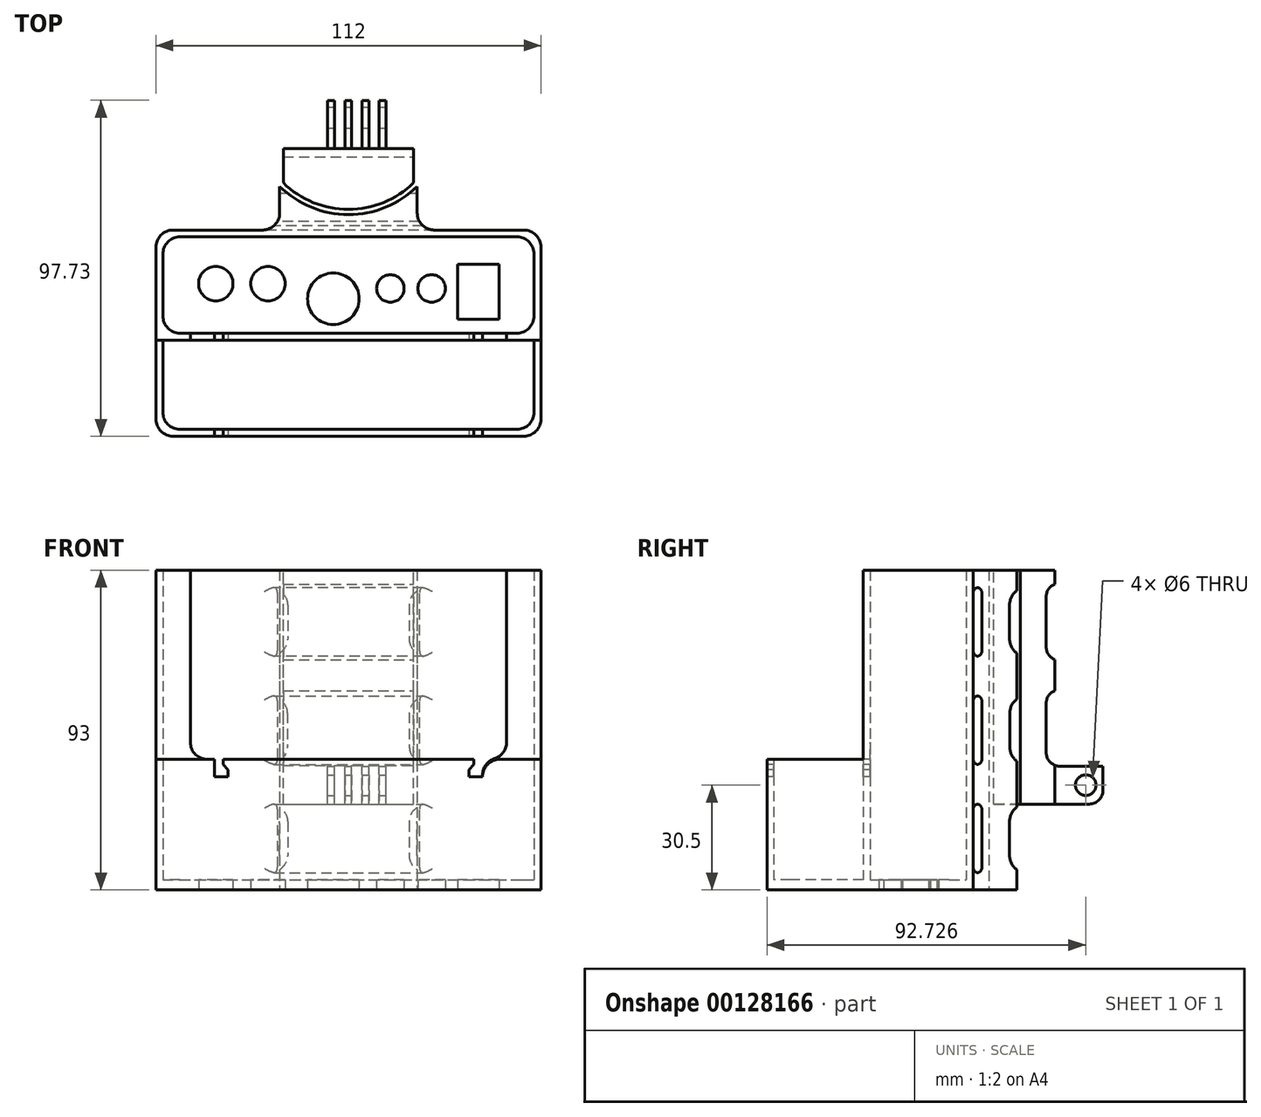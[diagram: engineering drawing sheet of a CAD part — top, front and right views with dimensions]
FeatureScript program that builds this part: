
annotation { "Feature Type Name" : "Feature", "Feature Type Description" : "" }
export const myFeature = defineFeature(function(context is Context, id is Id, definition is map)
    precondition{}
    {
        {
            var Q0;
            Q0=qCreatedBy(makeId("Top.planeOp"),FACE);
            var sketch = newSketch(context, id + "F0", { "sketchPlane" : qUnion([Q0])});
            skLineSegment(sketch, "E0.bottom", {"start": v(-47.35, 13.6) * mm, "end": v(60.65, 13.6) * mm});
            skLineSegment(sketch, "E0.top", {"start": v(-47.35, -14.4) * mm, "end": v(60.65, -14.4) * mm});
            skLineSegment(sketch, "E0.left", {"start": v(-47.35, 13.6) * mm, "end": v(-47.35, -14.4) * mm});
            skLineSegment(sketch, "E0.right", {"start": v(60.65, 13.6) * mm, "end": v(60.65, -14.4) * mm});
            skLineSegment(sketch, "E1.bottom", {"start": v(-49.35, 15.6) * mm, "end": v(62.65, 15.6) * mm});
            skLineSegment(sketch, "E1.top", {"start": v(-49.35, -16.4) * mm, "end": v(62.65, -16.4) * mm});
            skLineSegment(sketch, "E1.left", {"start": v(-49.35, 15.6) * mm, "end": v(-49.35, -16.4) * mm});
            skLineSegment(sketch, "E1.right", {"start": v(62.65, 15.6) * mm, "end": v(62.65, -16.4) * mm});
            skLineSegment(sketch, "E2", {"start": v(-49.35, -16.4) * mm, "end": v(-49.35, -44.4) * mm});
            skLineSegment(sketch, "E3", {"start": v(-49.35, -44.4) * mm, "end": v(62.65, -44.4) * mm});
            skLineSegment(sketch, "E4", {"start": v(62.65, -44.4) * mm, "end": v(62.65, -16.4) * mm});
            skLineSegment(sketch, "E5", {"start": v(-47.35, -16.4) * mm, "end": v(-47.35, -42.4) * mm});
            skLineSegment(sketch, "E6", {"start": v(-47.35, -42.4) * mm, "end": v(60.65, -42.4) * mm});
            skLineSegment(sketch, "E7", {"start": v(60.65, -42.4) * mm, "end": v(60.65, -16.4) * mm});
            skCircle(sketch, "E8", {"center": v(-31.95, 0) * mm, "radius": 5 * mm});
            skCircle(sketch, "E9", {"center": v(-16.75, 0) * mm, "radius": 5 * mm});
            skCircle(sketch, "E10", {"center": v(2.25, -4.4) * mm, "radius": 7.5 * mm});
            skCircle(sketch, "E11", {"center": v(30.85, -1.4) * mm, "radius": 4 * mm});
            skLineSegment(sketch, "E12.bottom", {"start": v(50.45, -10.4) * mm, "end": v(38.45, -10.4) * mm});
            skLineSegment(sketch, "E12.top", {"start": v(50.45, 5.6) * mm, "end": v(38.45, 5.6) * mm});
            skLineSegment(sketch, "E12.left", {"start": v(50.45, -10.4) * mm, "end": v(50.45, 5.6) * mm});
            skLineSegment(sketch, "E12.right", {"start": v(38.45, -10.4) * mm, "end": v(38.45, 5.6) * mm});
            skCircle(sketch, "E13", {"center": v(18.85, -1.4) * mm, "radius": 4 * mm});
            skLineSegment(sketch, "E14", {"start": v(6.65, 15.6) * mm, "end": v(6.65, 20.1) * mm});
            skLineSegment(sketch, "E15", {"start": v(-13.35, 28.25) * mm, "end": v(-13.35, 15.6) * mm});
            skArc(sketch, "E16", {"start": v(-13.35, 28.25) * mm, "mid": v(-4.15, 22.22) * mm, "end": v(6.65, 20.1) * mm});
            skArc(sketch, "E17.MirrorCS", {"start": v(26.65, 28.25) * mm, "mid": v(17.45, 22.22) * mm, "end": v(6.65, 20.1) * mm});
            skLineSegment(sketch, "E18.MirrorCS", {"start": v(26.65, 28.25) * mm, "end": v(26.65, 15.6) * mm});
            skSolve(sketch);
        }
        {
            var Q0;
            Q0=makeQuery(id+"F0.imprint","IMPRINT",FACE,{"disambiguationData":[TD([[makeQuery(id+"F0.imprint","IMPRINT",EDGE,{"derivedFrom":sQuery(id+"F0.wireOp",EDGE,"E0.bottom")}),-1.0]])]});
            var Q1;
            {var subQ0=sQuery(id+"F0.wireOp",EDGE,"E5");Q1=makeQuery(id+"F0.imprint","IMPRINT",FACE,{"disambiguationData":[TD([[makeQuery(id+"F0.imprint","IMPRINT",EDGE,{"derivedFrom":subQ0}),1.0]])]});}
            extrude(context, id + "F1", {"entities" : qUnion([Q0, Q1]), "depth" : 3 * mm});
        }
        {
            var Q0;
            Q0=makeQuery(id+"F0.imprint","IMPRINT",FACE,{"disambiguationData":[TD([[makeQuery(id+"F0.imprint","IMPRINT",EDGE,{"derivedFrom":sQuery(id+"F0.wireOp",EDGE,"E0.bottom")}),1.0]])]});
            var Q1;
            {var subQ0=sQuery(id+"F0.wireOp",EDGE,"E14");Q1=makeQuery(id+"F0.imprint","IMPRINT",FACE,{"disambiguationData":[TD([[makeQuery(id+"F0.imprint","IMPRINT",EDGE,{"derivedFrom":subQ0}),1.0]])]});}
            var Q2;
            {var subQ0=sQuery(id+"F0.wireOp",EDGE,"E14");Q2=makeQuery(id+"F0.imprint","IMPRINT",FACE,{"disambiguationData":[TD([[makeQuery(id+"F0.imprint","IMPRINT",EDGE,{"derivedFrom":subQ0}),-1.0]])]});}
            extrude(context, id + "F2", {"entities" : qUnion([Q0, Q1, Q2]), "operationType" : NewBodyOperationType.ADD, "depth" : 93 * mm});
        }
        {
            var Q0;
            Q0=makeQuery(id+"F2.opExtrude","SWEPT_FACE",FACE,{"disambiguationData":[OSD([sQuery(id+"F0.wireOp",EDGE,"E1.top")])]});
            var sketch = newSketch(context, id + "F3", { "sketchPlane" : qUnion([Q0])});
            skLineSegment(sketch, "E19.bottom", {"start": v(52.65, 93) * mm, "end": v(-39.35, 93) * mm});
            skLineSegment(sketch, "E19.top", {"start": v(52.65, 38) * mm, "end": v(-39.35, 38) * mm});
            skLineSegment(sketch, "E19.left", {"start": v(52.65, 93) * mm, "end": v(52.65, 38) * mm});
            skLineSegment(sketch, "E19.right", {"start": v(-39.35, 93) * mm, "end": v(-39.35, 38) * mm});
            skSolve(sketch);
        }
        {
            var Q0;
            Q0=makeQuery(id+"F3.imprint","IMPRINT",FACE,{"disambiguationData":[TD([[makeQuery(id+"F3.imprint","IMPRINT",EDGE,{"derivedFrom":sQuery(id+"F3.wireOp",EDGE,"E19.bottom")}),-1.0]])]});
            extrude(context, id + "F4", {"entities" : qUnion([Q0]), "operationType" : NewBodyOperationType.REMOVE, "oppositeDirection" : true, "depth" : 2 * mm});
        }
        {
            var Q0;
            {var subQ0=sQuery(id+"F0.wireOp",EDGE,"E2");Q0=makeQuery(id+"F0.imprint","IMPRINT",FACE,{"disambiguationData":[TD([[makeQuery(id+"F0.imprint","IMPRINT",EDGE,{"derivedFrom":subQ0}),1.0]])]});}
            extrude(context, id + "F5", {"entities" : qUnion([Q0]), "operationType" : NewBodyOperationType.ADD, "depth" : 38 * mm});
        }
        {
            var Q0;
            Q0=makeQuery(id+"F2.opExtrude","SWEPT_EDGE",EDGE,{"disambiguationData":[OSD([sQuery(id+"F0.wireOp",EDGE,"E1.bottom"),sQuery(id+"F0.wireOp",EDGE,"E1.left")])]});
            var Q1;
            Q1=makeQuery(id+"F2.opExtrude","SWEPT_EDGE",EDGE,{"disambiguationData":[OSD([sQuery(id+"F0.wireOp",EDGE,"E1.bottom"),sQuery(id+"F0.wireOp",EDGE,"E1.right")])]});
            var Q2;
            Q2=makeQuery(id+"F2.opExtrude","SWEPT_EDGE",EDGE,{"disambiguationData":[OSD([sQuery(id+"F0.wireOp",EDGE,"E0.bottom"),sQuery(id+"F0.wireOp",EDGE,"E0.left")])]});
            var Q3;
            Q3=makeQuery(id+"F2.opExtrude","SWEPT_EDGE",EDGE,{"disambiguationData":[OSD([sQuery(id+"F0.wireOp",EDGE,"E0.bottom"),sQuery(id+"F0.wireOp",EDGE,"E0.right")])]});
            var Q4;
            Q4=makeQuery(id+"F2.opExtrude","SWEPT_EDGE",EDGE,{"disambiguationData":[OSD([sQuery(id+"F0.wireOp",EDGE,"E0.top"),sQuery(id+"F0.wireOp",EDGE,"E0.left")])]});
            var Q5;
            Q5=makeQuery(id+"F2.opExtrude","SWEPT_EDGE",EDGE,{"disambiguationData":[OSD([sQuery(id+"F0.wireOp",EDGE,"E0.top"),sQuery(id+"F0.wireOp",EDGE,"E0.right")])]});
            var Q6;
            Q6=makeQuery(id+"F5.opExtrude","SWEPT_EDGE",EDGE,{"disambiguationData":[OSD([sQuery(id+"F0.wireOp",EDGE,"E1.top"),sQuery(id+"F0.wireOp",EDGE,"E5")])]});
            var Q7;
            Q7=makeQuery(id+"F5.opExtrude","SWEPT_EDGE",EDGE,{"disambiguationData":[OSD([sQuery(id+"F0.wireOp",EDGE,"E1.top"),sQuery(id+"F0.wireOp",EDGE,"E7")])]});
            var Q8;
            Q8=makeQuery(id+"F5.opExtrude","SWEPT_EDGE",EDGE,{"disambiguationData":[OSD([sQuery(id+"F0.wireOp",EDGE,"E6"),sQuery(id+"F0.wireOp",EDGE,"E7")])]});
            var Q9;
            Q9=makeQuery(id+"F5.opExtrude","SWEPT_EDGE",EDGE,{"disambiguationData":[OSD([sQuery(id+"F0.wireOp",EDGE,"E5"),sQuery(id+"F0.wireOp",EDGE,"E6")])]});
            var Q10;
            Q10=makeQuery(id+"F5.opExtrude","SWEPT_EDGE",EDGE,{"disambiguationData":[OSD([sQuery(id+"F0.wireOp",EDGE,"E3"),sQuery(id+"F0.wireOp",EDGE,"E4")])]});
            var Q11;
            Q11=makeQuery(id+"F5.opExtrude","SWEPT_EDGE",EDGE,{"disambiguationData":[OSD([sQuery(id+"F0.wireOp",EDGE,"E2"),sQuery(id+"F0.wireOp",EDGE,"E3")])]});
            var Q12;
            Q12=makeQuery(id+"F4.boolean.opBoolean","COPY",EDGE,{"derivedFrom":makeQuery(id+"F4.opExtrude","SWEPT_EDGE",EDGE,{"disambiguationData":[OSD([sQuery(id+"F3.wireOp",EDGE,"E19.top"),sQuery(id+"F3.wireOp",EDGE,"E19.left")])]})});
            var Q13;
            Q13=makeQuery(id+"F4.boolean.opBoolean","COPY",EDGE,{"derivedFrom":makeQuery(id+"F4.opExtrude","SWEPT_EDGE",EDGE,{"disambiguationData":[OSD([sQuery(id+"F3.wireOp",EDGE,"E19.top"),sQuery(id+"F3.wireOp",EDGE,"E19.right")])]})});
            var Q14;
            {var subQ0=sQuery(id+"F0.wireOp",EDGE,"E1.top");Q14=makeQuery(id+"F5.opExtrude","CAP_EDGE",EDGE,{"disambiguationData":[OSD([subQ0]),TDD([makeQuery(id+"F0.imprint","IMPRINT",EDGE,{"disambiguationData":[TD([[makeQuery(id+"F0.imprint","INTERSECT",VERTEX,{"derivedFrom":[subQ0,sQuery(id+"F0.wireOp",EDGE,"E7")]}),-1.0]])],"derivedFrom":subQ0})])],"isStart":false});}
            var Q15;
            {var subQ0=sQuery(id+"F0.wireOp",EDGE,"E1.top");Q15=makeQuery(id+"F5.opExtrude","CAP_EDGE",EDGE,{"disambiguationData":[OSD([subQ0]),TDD([makeQuery(id+"F0.imprint","IMPRINT",EDGE,{"disambiguationData":[TD([[makeQuery(id+"F0.imprint","INTERSECT",VERTEX,{"derivedFrom":[subQ0,sQuery(id+"F0.wireOp",EDGE,"E5")]}),1.0]])],"derivedFrom":subQ0})])],"isStart":false});}
            fillet(context, id + "F6", {"entities" : qUnion([Q0, Q1, Q2, Q3, Q4, Q5, Q6, Q7, Q8, Q9, Q10, Q11, Q12, Q13, Q14, Q15]), "radius" : 5 * mm, "tangentPropagation" : true, "allowEdgeOverflow" : false});
        }
        {
            var Q0;
            Q0=makeQuery(id+"F5.opExtrude","SWEPT_FACE",FACE,{"disambiguationData":[OSD([sQuery(id+"F0.wireOp",EDGE,"E3")])]});
            var sketch = newSketch(context, id + "F7", { "sketchPlane" : qUnion([Q0])});
            skLineSegment(sketch, "E20", {"start": v(-32.35, 38) * mm, "end": v(-32.35, 33) * mm});
            skLineSegment(sketch, "E21", {"start": v(-32.35, 33) * mm, "end": v(-28.35, 33) * mm});
            skLineSegment(sketch, "E22", {"start": v(-28.35, 33) * mm, "end": v(-28.35, 35) * mm});
            skLineSegment(sketch, "E23", {"start": v(-28.35, 35) * mm, "end": v(-29.85, 36.5) * mm});
            skLineSegment(sketch, "E24", {"start": v(-29.85, 36.5) * mm, "end": v(-29.85, 38) * mm});
            skLineSegment(sketch, "E25", {"start": v(6.65, 33) * mm, "end": v(6.65, 38) * mm});
            skLineSegment(sketch, "E26.MirrorCS", {"start": v(41.65, 35) * mm, "end": v(43.15, 36.5) * mm});
            skLineSegment(sketch, "E27.MirrorCS", {"start": v(43.15, 36.5) * mm, "end": v(43.15, 38) * mm});
            skLineSegment(sketch, "E28.MirrorCS", {"start": v(41.65, 33) * mm, "end": v(41.65, 35) * mm});
            skLineSegment(sketch, "E29.MirrorCS", {"start": v(45.65, 33) * mm, "end": v(41.65, 33) * mm});
            skLineSegment(sketch, "E30.MirrorCS", {"start": v(45.65, 38) * mm, "end": v(45.65, 33) * mm});
            skSolve(sketch);
        }
        {
            var Q0;
            {var subQ0=sQuery(id+"F7.wireOp",EDGE,"E20");Q0=makeQuery(id+"F7.imprint","IMPRINT",FACE,{"disambiguationData":[TD([[makeQuery(id+"F7.imprint","IMPRINT",EDGE,{"derivedFrom":subQ0}),1.0]])]});}
            var Q1;
            Q1=makeQuery(id+"F7.imprint","IMPRINT",FACE,{"disambiguationData":[TD([[makeQuery(id+"F7.imprint","IMPRINT",EDGE,{"derivedFrom":sQuery(id+"F7.wireOp",EDGE,"E26.MirrorCS")}),-1.0]])]});
            extrude(context, id + "F8", {"entities" : qUnion([Q0, Q1]), "operationType" : NewBodyOperationType.REMOVE, "oppositeDirection" : true, "depth" : 40 * mm});
        }
        {
            var Q0;
            Q0=makeQuery(id+"F8.boolean.opBoolean","COPY",EDGE,{"disambiguationData":[OD(0.0)],"derivedFrom":makeQuery(id+"F8.opExtrude","SWEPT_EDGE",EDGE,{"disambiguationData":[OSD([sQuery(id+"F0.wireOp",EDGE,"E3"),sQuery(id+"F7.wireOp",EDGE,"E20")])]})});
            var Q1;
            Q1=makeQuery(id+"F8.boolean.opBoolean","COPY",EDGE,{"disambiguationData":[OD(1.0)],"derivedFrom":makeQuery(id+"F8.opExtrude","SWEPT_EDGE",EDGE,{"disambiguationData":[OSD([sQuery(id+"F0.wireOp",EDGE,"E3"),sQuery(id+"F7.wireOp",EDGE,"E20")])]})});
            var Q2;
            Q2=makeQuery(id+"F8.boolean.opBoolean","COPY",EDGE,{"disambiguationData":[OD(0.0)],"derivedFrom":makeQuery(id+"F8.opExtrude","SWEPT_EDGE",EDGE,{"disambiguationData":[OSD([sQuery(id+"F0.wireOp",EDGE,"E3"),sQuery(id+"F7.wireOp",EDGE,"E30.MirrorCS")])]})});
            var Q3;
            Q3=makeQuery(id+"F8.boolean.opBoolean","COPY",EDGE,{"disambiguationData":[OD(1.0)],"derivedFrom":makeQuery(id+"F8.opExtrude","SWEPT_EDGE",EDGE,{"disambiguationData":[OSD([sQuery(id+"F0.wireOp",EDGE,"E3"),sQuery(id+"F7.wireOp",EDGE,"E30.MirrorCS")])]})});
            fillet(context, id + "F9", {"entities" : qUnion([Q0, Q1, Q2, Q3]), "radius" : 5 * mm, "tangentPropagation" : true, "allowEdgeOverflow" : false});
        }
        {
            var Q0;
            Q0=makeQuery(id+"F2.opExtrude","SWEPT_FACE",FACE,{"disambiguationData":[OSD([sQuery(id+"F0.wireOp",EDGE,"E15")])]});
            var sketch = newSketch(context, id + "F10", { "sketchPlane" : qUnion([Q0])});
            skLineSegment(sketch, "E31", {"start": v(-15.6, 46.5) * mm, "end": v(-18.1, 46.5) * mm});
            skPoint(sketch, "E31.endSnap0", {"position": v(-15.6, 46.5) * mm});
            skLineSegment(sketch, "E32", {"start": v(-18.1, 46.5) * mm, "end": v(-18.1, 36.5) * mm});
            skLineSegment(sketch, "E33", {"start": v(-18.1, 36.5) * mm, "end": v(-15.6, 36.5) * mm});
            skLineSegment(sketch, "E34", {"start": v(-15.6, 5) * mm, "end": v(-18.1, 5) * mm});
            skLineSegment(sketch, "E35", {"start": v(-18.1, 5) * mm, "end": v(-18.1, 25) * mm});
            skLineSegment(sketch, "E36", {"start": v(-18.1, 25) * mm, "end": v(-15.6, 25) * mm});
            skLineSegment(sketch, "E37.MirrorCS", {"start": v(-18.1, 46.5) * mm, "end": v(-18.1, 56.5) * mm});
            skLineSegment(sketch, "E38.MirrorCS", {"start": v(-18.1, 56.5) * mm, "end": v(-15.6, 56.5) * mm});
            skLineSegment(sketch, "E39.MirrorCS", {"start": v(-18.1, 88) * mm, "end": v(-18.1, 68) * mm});
            skLineSegment(sketch, "E40.MirrorCS", {"start": v(-18.1, 68) * mm, "end": v(-15.6, 68) * mm});
            skLineSegment(sketch, "E41.MirrorCS", {"start": v(-15.6, 88) * mm, "end": v(-18.1, 88) * mm});
            skLineSegment(sketch, "E42", {"start": v(-28.25, 46.5) * mm, "end": v(-26.25, 46.5) * mm});
            skLineSegment(sketch, "E43", {"start": v(-26.25, 46.5) * mm, "end": v(-26.25, 36.5) * mm});
            skLineSegment(sketch, "E44", {"start": v(-26.25, 36.5) * mm, "end": v(-28.25, 36.5) * mm});
            skLineSegment(sketch, "E45", {"start": v(-28.25, 25) * mm, "end": v(-26.18, 25) * mm});
            skLineSegment(sketch, "E46", {"start": v(-26.18, 25) * mm, "end": v(-26.18, 5) * mm});
            skLineSegment(sketch, "E47", {"start": v(-26.18, 5) * mm, "end": v(-28.25, 5) * mm});
            skLineSegment(sketch, "E48.MirrorCS", {"start": v(-26.25, 56.5) * mm, "end": v(-28.25, 56.5) * mm});
            skLineSegment(sketch, "E49.MirrorCS", {"start": v(-26.25, 46.5) * mm, "end": v(-26.25, 56.5) * mm});
            skLineSegment(sketch, "E50.MirrorCS", {"start": v(-26.18, 68) * mm, "end": v(-26.18, 88) * mm});
            skLineSegment(sketch, "E51.MirrorCS", {"start": v(-26.18, 88) * mm, "end": v(-28.25, 88) * mm});
            skLineSegment(sketch, "E52.MirrorCS", {"start": v(-28.25, 68) * mm, "end": v(-26.18, 68) * mm});
            skSolve(sketch);
        }
        {
            var Q0;
            {var subQ0=sQuery(id+"F10.wireOp",EDGE,"E34");Q0=makeQuery(id+"F10.imprint","IMPRINT",FACE,{"disambiguationData":[TD([[makeQuery(id+"F10.imprint","IMPRINT",EDGE,{"derivedFrom":subQ0}),-1.0]])]});}
            var Q1;
            {var subQ0=sQuery(id+"F10.wireOp",EDGE,"E31");Q1=makeQuery(id+"F10.imprint","IMPRINT",FACE,{"disambiguationData":[TD([[makeQuery(id+"F10.imprint","IMPRINT",EDGE,{"derivedFrom":subQ0}),1.0]])]});}
            var Q2;
            {var subQ0=sQuery(id+"F10.wireOp",EDGE,"E31");Q2=makeQuery(id+"F10.imprint","IMPRINT",FACE,{"disambiguationData":[TD([[makeQuery(id+"F10.imprint","IMPRINT",EDGE,{"derivedFrom":subQ0}),-1.0]])]});}
            var Q3;
            Q3=makeQuery(id+"F10.imprint","IMPRINT",FACE,{"disambiguationData":[TD([[makeQuery(id+"F10.imprint","IMPRINT",EDGE,{"derivedFrom":sQuery(id+"F10.wireOp",EDGE,"E39.MirrorCS")}),1.0]])]});
            var Q4;
            {var subQ0=sQuery(id+"F10.wireOp",EDGE,"E42");Q4=makeQuery(id+"F10.imprint","IMPRINT",FACE,{"disambiguationData":[TD([[makeQuery(id+"F10.imprint","IMPRINT",EDGE,{"derivedFrom":subQ0}),1.0]])]});}
            var Q5;
            {var subQ0=sQuery(id+"F10.wireOp",EDGE,"E42");Q5=makeQuery(id+"F10.imprint","IMPRINT",FACE,{"disambiguationData":[TD([[makeQuery(id+"F10.imprint","IMPRINT",EDGE,{"derivedFrom":subQ0}),-1.0]])]});}
            var Q6;
            {var subQ0=sQuery(id+"F10.wireOp",EDGE,"E45");Q6=makeQuery(id+"F10.imprint","IMPRINT",FACE,{"disambiguationData":[TD([[makeQuery(id+"F10.imprint","IMPRINT",EDGE,{"derivedFrom":subQ0}),-1.0]])]});}
            var Q7;
            Q7=makeQuery(id+"F10.imprint","IMPRINT",FACE,{"disambiguationData":[TD([[makeQuery(id+"F10.imprint","IMPRINT",EDGE,{"derivedFrom":sQuery(id+"F10.wireOp",EDGE,"E50.MirrorCS")}),1.0]])]});
            extrude(context, id + "F11", {"entities" : qUnion([Q0, Q1, Q2, Q3, Q4, Q5, Q6, Q7]), "operationType" : NewBodyOperationType.REMOVE, "endBound" : BoundingType.SYMMETRIC, "oppositeDirection" : true, "depth" : 100 * mm});
        }
        {
            var Q0;
            {var subQ0=sQuery(id+"F10.wireOp",EDGE,"E34");var subQ1=sQuery(id+"F0.wireOp",EDGE,"E15");var subQ2=sQuery(id+"F0.wireOp",EDGE,"E1.bottom");var subQ3=makeQuery(id+"F2.opExtrude","SWEPT_EDGE",EDGE,{"disambiguationData":[OSD([subQ2,subQ1])]});Q0=makeQuery(id+"F11.boolean.opBoolean","SPLIT",EDGE,{"disambiguationData":[TD([makeQuery(id+"F11.opExtrude","SWEPT_FACE",FACE,{"disambiguationData":[OSD([subQ0])]})])],"derivedFrom":subQ3});}
            var Q1;
            {var subQ0=sQuery(id+"F10.wireOp",EDGE,"E33");var subQ2=sQuery(id+"F0.wireOp",EDGE,"E1.bottom");var subQ4=sQuery(id+"F0.wireOp",EDGE,"E18.MirrorCS");Q1=makeQuery(id+"F11.boolean.opBoolean","SPLIT",EDGE,{"disambiguationData":[TD([makeQuery(id+"F11.opExtrude","SWEPT_FACE",FACE,{"disambiguationData":[OSD([subQ0])]})])],"derivedFrom":makeQuery(id+"F2.opExtrude","SWEPT_EDGE",EDGE,{"disambiguationData":[OSD([subQ2,subQ4])]})});}
            var Q2;
            Q2=makeQuery(id+"F11.boolean.opBoolean","COPY",EDGE,{"disambiguationData":[OD(0.0)],"derivedFrom":makeQuery(id+"F11.opExtrude","SWEPT_EDGE",EDGE,{"disambiguationData":[OSD([sQuery(id+"F10.wireOp",EDGE,"E46"),sQuery(id+"F10.wireOp",EDGE,"E47")])]})});
            var Q3;
            Q3=makeQuery(id+"F11.boolean.opBoolean","COPY",EDGE,{"disambiguationData":[OD(1.0)],"derivedFrom":makeQuery(id+"F11.opExtrude","SWEPT_EDGE",EDGE,{"disambiguationData":[OSD([sQuery(id+"F10.wireOp",EDGE,"E46"),sQuery(id+"F10.wireOp",EDGE,"E47")])]})});
            var Q4;
            Q4=makeQuery(id+"F11.boolean.opBoolean","COPY",EDGE,{"disambiguationData":[OD(1.0)],"derivedFrom":makeQuery(id+"F11.opExtrude","SWEPT_EDGE",EDGE,{"disambiguationData":[OSD([sQuery(id+"F10.wireOp",EDGE,"E43"),sQuery(id+"F10.wireOp",EDGE,"E44")])]})});
            var Q5;
            Q5=makeQuery(id+"F11.boolean.opBoolean","COPY",EDGE,{"disambiguationData":[OD(1.0)],"derivedFrom":makeQuery(id+"F11.opExtrude","SWEPT_EDGE",EDGE,{"disambiguationData":[OSD([sQuery(id+"F10.wireOp",EDGE,"E50.MirrorCS"),sQuery(id+"F10.wireOp",EDGE,"E52.MirrorCS")])]})});
            var Q6;
            Q6=makeQuery(id+"F11.boolean.opBoolean","COPY",EDGE,{"disambiguationData":[OD(0.0)],"derivedFrom":makeQuery(id+"F11.opExtrude","SWEPT_EDGE",EDGE,{"disambiguationData":[OSD([sQuery(id+"F10.wireOp",EDGE,"E50.MirrorCS"),sQuery(id+"F10.wireOp",EDGE,"E52.MirrorCS")])]})});
            var Q7;
            Q7=makeQuery(id+"F11.boolean.opBoolean","COPY",EDGE,{"disambiguationData":[OD(0.0)],"derivedFrom":makeQuery(id+"F11.opExtrude","SWEPT_EDGE",EDGE,{"disambiguationData":[OSD([sQuery(id+"F10.wireOp",EDGE,"E43"),sQuery(id+"F10.wireOp",EDGE,"E44")])]})});
            var Q8;
            Q8=makeQuery(id+"F11.boolean.opBoolean","COPY",EDGE,{"disambiguationData":[OD(0.0)],"derivedFrom":makeQuery(id+"F11.opExtrude","SWEPT_EDGE",EDGE,{"disambiguationData":[OSD([sQuery(id+"F10.wireOp",EDGE,"E45"),sQuery(id+"F10.wireOp",EDGE,"E46")])]})});
            var Q9;
            Q9=makeQuery(id+"F11.boolean.opBoolean","COPY",EDGE,{"disambiguationData":[OD(1.0)],"derivedFrom":makeQuery(id+"F11.opExtrude","SWEPT_EDGE",EDGE,{"disambiguationData":[OSD([sQuery(id+"F10.wireOp",EDGE,"E45"),sQuery(id+"F10.wireOp",EDGE,"E46")])]})});
            var Q10;
            Q10=makeQuery(id+"F11.boolean.opBoolean","COPY",EDGE,{"disambiguationData":[OD(1.0)],"derivedFrom":makeQuery(id+"F11.opExtrude","SWEPT_EDGE",EDGE,{"disambiguationData":[OSD([sQuery(id+"F10.wireOp",EDGE,"E48.MirrorCS"),sQuery(id+"F10.wireOp",EDGE,"E49.MirrorCS")])]})});
            var Q11;
            Q11=makeQuery(id+"F11.boolean.opBoolean","COPY",EDGE,{"disambiguationData":[OD(0.0)],"derivedFrom":makeQuery(id+"F11.opExtrude","SWEPT_EDGE",EDGE,{"disambiguationData":[OSD([sQuery(id+"F10.wireOp",EDGE,"E48.MirrorCS"),sQuery(id+"F10.wireOp",EDGE,"E49.MirrorCS")])]})});
            var Q12;
            Q12=makeQuery(id+"F11.boolean.opBoolean","COPY",EDGE,{"disambiguationData":[OD(0.0)],"derivedFrom":makeQuery(id+"F11.opExtrude","SWEPT_EDGE",EDGE,{"disambiguationData":[OSD([sQuery(id+"F10.wireOp",EDGE,"E50.MirrorCS"),sQuery(id+"F10.wireOp",EDGE,"E51.MirrorCS")])]})});
            var Q13;
            Q13=makeQuery(id+"F11.boolean.opBoolean","COPY",EDGE,{"disambiguationData":[OD(1.0)],"derivedFrom":makeQuery(id+"F11.opExtrude","SWEPT_EDGE",EDGE,{"disambiguationData":[OSD([sQuery(id+"F10.wireOp",EDGE,"E50.MirrorCS"),sQuery(id+"F10.wireOp",EDGE,"E51.MirrorCS")])]})});
            fillet(context, id + "F12", {"entities" : qUnion([Q0, Q1, Q2, Q3, Q4, Q5, Q6, Q7, Q8, Q9, Q10, Q11, Q12, Q13]), "radius" : 5 * mm, "tangentPropagation" : true, "allowEdgeOverflow" : false});
        }
        {
            var Q0;
            Q0=makeQuery(id+"F11.boolean.opBoolean","COPY",EDGE,{"derivedFrom":makeQuery(id+"F11.opExtrude","SWEPT_EDGE",EDGE,{"disambiguationData":[OSD([sQuery(id+"F0.wireOp",EDGE,"E1.bottom"),sQuery(id+"F0.wireOp",EDGE,"E15"),sQuery(id+"F10.wireOp",EDGE,"E34")])]})});
            var Q1;
            Q1=makeQuery(id+"F11.boolean.opBoolean","COPY",EDGE,{"disambiguationData":[OD(0.0)],"derivedFrom":makeQuery(id+"F11.opExtrude","SWEPT_EDGE",EDGE,{"disambiguationData":[OSD([sQuery(id+"F10.wireOp",EDGE,"E34"),sQuery(id+"F10.wireOp",EDGE,"E35")])]})});
            var Q2;
            Q2=makeQuery(id+"F11.boolean.opBoolean","COPY",EDGE,{"disambiguationData":[OD(0.0)],"derivedFrom":makeQuery(id+"F11.opExtrude","SWEPT_EDGE",EDGE,{"disambiguationData":[OSD([sQuery(id+"F10.wireOp",EDGE,"E32"),sQuery(id+"F10.wireOp",EDGE,"E33")])]})});
            var Q3;
            Q3=makeQuery(id+"F11.boolean.opBoolean","COPY",EDGE,{"derivedFrom":makeQuery(id+"F11.opExtrude","SWEPT_EDGE",EDGE,{"disambiguationData":[OSD([sQuery(id+"F0.wireOp",EDGE,"E1.bottom"),sQuery(id+"F0.wireOp",EDGE,"E15"),sQuery(id+"F10.wireOp",EDGE,"E33")])]})});
            var Q4;
            Q4=makeQuery(id+"F11.boolean.opBoolean","COPY",EDGE,{"derivedFrom":makeQuery(id+"F11.opExtrude","SWEPT_EDGE",EDGE,{"disambiguationData":[OSD([sQuery(id+"F0.wireOp",EDGE,"E1.bottom"),sQuery(id+"F0.wireOp",EDGE,"E15"),sQuery(id+"F10.wireOp",EDGE,"E36")])]})});
            var Q5;
            Q5=makeQuery(id+"F11.boolean.opBoolean","COPY",EDGE,{"disambiguationData":[OD(1.0)],"derivedFrom":makeQuery(id+"F11.opExtrude","SWEPT_EDGE",EDGE,{"disambiguationData":[OSD([sQuery(id+"F10.wireOp",EDGE,"E35"),sQuery(id+"F10.wireOp",EDGE,"E36")])]})});
            var Q6;
            Q6=makeQuery(id+"F11.boolean.opBoolean","COPY",EDGE,{"derivedFrom":makeQuery(id+"F11.opExtrude","SWEPT_EDGE",EDGE,{"disambiguationData":[OSD([sQuery(id+"F0.wireOp",EDGE,"E1.bottom"),sQuery(id+"F0.wireOp",EDGE,"E15"),sQuery(id+"F10.wireOp",EDGE,"E38.MirrorCS")])]})});
            var Q7;
            Q7=makeQuery(id+"F11.boolean.opBoolean","COPY",EDGE,{"disambiguationData":[OD(0.0)],"derivedFrom":makeQuery(id+"F11.opExtrude","SWEPT_EDGE",EDGE,{"disambiguationData":[OSD([sQuery(id+"F10.wireOp",EDGE,"E37.MirrorCS"),sQuery(id+"F10.wireOp",EDGE,"E38.MirrorCS")])]})});
            var Q8;
            Q8=makeQuery(id+"F11.boolean.opBoolean","COPY",EDGE,{"derivedFrom":makeQuery(id+"F11.opExtrude","SWEPT_EDGE",EDGE,{"disambiguationData":[OSD([sQuery(id+"F0.wireOp",EDGE,"E1.bottom"),sQuery(id+"F0.wireOp",EDGE,"E15"),sQuery(id+"F10.wireOp",EDGE,"E40.MirrorCS")])]})});
            var Q9;
            Q9=makeQuery(id+"F11.boolean.opBoolean","COPY",EDGE,{"derivedFrom":makeQuery(id+"F11.opExtrude","SWEPT_EDGE",EDGE,{"disambiguationData":[OSD([sQuery(id+"F0.wireOp",EDGE,"E1.bottom"),sQuery(id+"F0.wireOp",EDGE,"E15"),sQuery(id+"F10.wireOp",EDGE,"E41.MirrorCS")])]})});
            var Q10;
            Q10=makeQuery(id+"F11.boolean.opBoolean","COPY",EDGE,{"disambiguationData":[OD(0.0)],"derivedFrom":makeQuery(id+"F11.opExtrude","SWEPT_EDGE",EDGE,{"disambiguationData":[OSD([sQuery(id+"F10.wireOp",EDGE,"E39.MirrorCS"),sQuery(id+"F10.wireOp",EDGE,"E41.MirrorCS")])]})});
            var Q11;
            Q11=makeQuery(id+"F11.boolean.opBoolean","COPY",EDGE,{"disambiguationData":[OD(0.0)],"derivedFrom":makeQuery(id+"F11.opExtrude","SWEPT_EDGE",EDGE,{"disambiguationData":[OSD([sQuery(id+"F10.wireOp",EDGE,"E39.MirrorCS"),sQuery(id+"F10.wireOp",EDGE,"E40.MirrorCS")])]})});
            fillet(context, id + "F13", {"entities" : qUnion([Q0, Q1, Q2, Q3, Q4, Q5, Q6, Q7, Q8, Q9, Q10, Q11]), "radius" : 1.5 * mm, "tangentPropagation" : true, "allowEdgeOverflow" : false});
        }
        {
            var Q0;
            Q0=makeQuery(id+"F2.opExtrude","CAP_FACE",FACE,{"disambiguationData":[OSD([sQuery(id+"F0.wireOp",EDGE,"E0.bottom"),sQuery(id+"F0.wireOp",EDGE,"E0.top"),sQuery(id+"F0.wireOp",EDGE,"E0.left"),sQuery(id+"F0.wireOp",EDGE,"E0.right"),sQuery(id+"F0.wireOp",EDGE,"E1.bottom"),sQuery(id+"F0.wireOp",EDGE,"E1.top"),sQuery(id+"F0.wireOp",EDGE,"E1.left"),sQuery(id+"F0.wireOp",EDGE,"E1.right"),sQuery(id+"F0.wireOp",EDGE,"E15"),sQuery(id+"F0.wireOp",EDGE,"E16"),sQuery(id+"F0.wireOp",EDGE,"E17.MirrorCS"),sQuery(id+"F0.wireOp",EDGE,"E18.MirrorCS")])],"isStart":false});
            var sketch = newSketch(context, id + "F14", { "sketchPlane" : qUnion([Q0])});
            skArc(sketch, "E53.0", {"start": v(25.6, 29.33) * mm, "mid": v(16.88, 23.6) * mm, "end": v(6.65, 21.6) * mm});
            skArc(sketch, "E53.1", {"start": v(-12.3, 29.33) * mm, "mid": v(-3.59, 23.6) * mm, "end": v(6.65, 21.6) * mm});
            skLineSegment(sketch, "E54", {"start": v(-12.3, 29.33) * mm, "end": v(-12.3, 39.33) * mm});
            skLineSegment(sketch, "E55", {"start": v(-12.3, 39.33) * mm, "end": v(25.6, 39.33) * mm});
            skLineSegment(sketch, "E56", {"start": v(25.6, 39.33) * mm, "end": v(25.6, 29.33) * mm});
            skSolve(sketch);
        }
        {
            var Q0;
            Q0 = qSketchRegion(id + "F14", true);
            var Q1;
            Q1=makeQuery(id+"F14.imprint","IMPRINT",FACE,{"disambiguationData":[TD([[makeQuery(id+"F14.imprint","IMPRINT",EDGE,{"derivedFrom":sQuery(id+"F14.wireOp",EDGE,"E53.0")}),-1.0]])]});
            extrude(context, id + "F15", {"entities" : qUnion([Q0, Q1]), "oppositeDirection" : true, "depth" : 68 * mm});
        }
        {
            var Q0;
            Q0=makeQuery(id+"F15.opExtrude","SWEPT_FACE",FACE,{"disambiguationData":[OSD([sQuery(id+"F14.wireOp",EDGE,"E56")])]});
            var sketch = newSketch(context, id + "F16", { "sketchPlane" : qUnion([Q0])});
            skLineSegment(sketch, "E57", {"start": v(39.33, 25) * mm, "end": v(53.33, 25) * mm});
            skLineSegment(sketch, "E58", {"start": v(53.33, 25) * mm, "end": v(53.33, 36) * mm});
            skLineSegment(sketch, "E59", {"start": v(53.33, 36) * mm, "end": v(39.33, 36) * mm});
            skPoint(sketch, "E60", {"position": v(48.33, 30.5) * mm});
            skPoint(sketch, "E60.positionSnap0", {"position": v(53.33, 30.5) * mm});
            skCircle(sketch, "E61", {"center": v(48.33, 30.5) * mm, "radius": 3 * mm});
            skLineSegment(sketch, "E62", {"start": v(39.33, 89) * mm, "end": v(36.83, 89) * mm});
            skLineSegment(sketch, "E63", {"start": v(36.83, 89) * mm, "end": v(36.83, 67) * mm});
            skLineSegment(sketch, "E64", {"start": v(36.83, 67) * mm, "end": v(39.33, 67) * mm});
            skLineSegment(sketch, "E65", {"start": v(39.33, 58) * mm, "end": v(36.83, 58) * mm});
            skLineSegment(sketch, "E66", {"start": v(36.83, 58) * mm, "end": v(36.83, 36) * mm});
            skLineSegment(sketch, "E67", {"start": v(36.83, 36) * mm, "end": v(39.33, 36) * mm});
            skSolve(sketch);
        }
        {
            var Q0;
            {var subQ1=sQuery(id+"F16.wireOp",EDGE,"E57");Q0=makeQuery(id+"F16.imprint","IMPRINT",FACE,{"disambiguationData":[TD([[makeQuery(id+"F16.imprint","IMPRINT",EDGE,{"derivedFrom":subQ1}),1.0]])]});}
            extrude(context, id + "F17", {"entities" : qUnion([Q0]), "operationType" : NewBodyOperationType.ADD, "oppositeDirection" : true, "depth" : 25 * mm, "hasSecondDirection" : true, "secondDirectionOppositeDirection" : true, "secondDirectionDepth" : 8 * mm});
        }
        {
            var Q0;
            Q0=makeQuery(id+"F17.opExtrude","SWEPT_EDGE",EDGE,{"disambiguationData":[OSD([sQuery(id+"F16.wireOp",EDGE,"E57"),sQuery(id+"F16.wireOp",EDGE,"E58")])]});
            fillet(context, id + "F18", {"entities" : qUnion([Q0]), "radius" : 4 * mm, "tangentPropagation" : true, "allowEdgeOverflow" : false});
        }
        {
            var Q0;
            Q0=makeQuery(id+"F17.opExtrude","SWEPT_FACE",FACE,{"disambiguationData":[OSD([sQuery(id+"F16.wireOp",EDGE,"E59")])]});
            var sketch = newSketch(context, id + "F19", { "sketchPlane" : qUnion([Q0])});
            skLineSegment(sketch, "E68", {"start": v(2.6, 39.33) * mm, "end": v(2.6, 53.33) * mm});
            skLineSegment(sketch, "E69", {"start": v(5.6, 53.33) * mm, "end": v(5.6, 39.33) * mm});
            skLineSegment(sketch, "E70", {"start": v(15.6, 53.33) * mm, "end": v(15.6, 39.33) * mm});
            skLineSegment(sketch, "E71", {"start": v(12.6, 53.33) * mm, "end": v(12.6, 39.33) * mm});
            skLineSegment(sketch, "E72", {"start": v(7.6, 53.33) * mm, "end": v(7.6, 39.33) * mm});
            skLineSegment(sketch, "E73", {"start": v(10.6, 53.33) * mm, "end": v(10.6, 39.33) * mm});
            skSolve(sketch);
        }
        {
            var Q0;
            {var subQ0=sQuery(id+"F19.wireOp",EDGE,"E68");Q0=makeQuery(id+"F19.imprint","IMPRINT",FACE,{"disambiguationData":[TD([[makeQuery(id+"F19.imprint","IMPRINT",EDGE,{"derivedFrom":subQ0}),-1.0]])]});}
            var Q1;
            {var subQ0=sQuery(id+"F19.wireOp",EDGE,"E72");Q1=makeQuery(id+"F19.imprint","IMPRINT",FACE,{"disambiguationData":[TD([[makeQuery(id+"F19.imprint","IMPRINT",EDGE,{"derivedFrom":subQ0}),1.0]])]});}
            var Q2;
            {var subQ0=sQuery(id+"F19.wireOp",EDGE,"E70");Q2=makeQuery(id+"F19.imprint","IMPRINT",FACE,{"disambiguationData":[TD([[makeQuery(id+"F19.imprint","IMPRINT",EDGE,{"derivedFrom":subQ0}),-1.0]])]});}
            extrude(context, id + "F20", {"entities" : qUnion([Q0, Q1, Q2]), "operationType" : NewBodyOperationType.REMOVE, "oppositeDirection" : true, "depth" : 13 * mm});
        }
        {
            var Q0;
            {var subQ0=sQuery(id+"F16.wireOp",EDGE,"E62");Q0=makeQuery(id+"F16.imprint","IMPRINT",FACE,{"disambiguationData":[TD([[makeQuery(id+"F16.imprint","IMPRINT",EDGE,{"derivedFrom":subQ0}),1.0]])]});}
            var Q1;
            {var subQ0=sQuery(id+"F16.wireOp",EDGE,"E65");Q1=makeQuery(id+"F16.imprint","IMPRINT",FACE,{"disambiguationData":[TD([[makeQuery(id+"F16.imprint","IMPRINT",EDGE,{"derivedFrom":subQ0}),1.0]])]});}
            extrude(context, id + "F21", {"entities" : qUnion([Q0, Q1]), "operationType" : NewBodyOperationType.REMOVE, "endBound" : BoundingType.UP_TO_NEXT, "oppositeDirection" : true, "depth" : 25 * mm});
        }
        {
            var Q0;
            Q0=makeQuery(id+"F21.boolean.opBoolean","COPY",EDGE,{"derivedFrom":makeQuery(id+"F21.opExtrude","SWEPT_EDGE",EDGE,{"disambiguationData":[OSD([sQuery(id+"F16.wireOp",EDGE,"E62"),sQuery(id+"F16.wireOp",EDGE,"E63")])]})});
            var Q1;
            Q1=makeQuery(id+"F21.boolean.opBoolean","COPY",EDGE,{"derivedFrom":makeQuery(id+"F21.opExtrude","SWEPT_EDGE",EDGE,{"disambiguationData":[OSD([sQuery(id+"F16.wireOp",EDGE,"E63"),sQuery(id+"F16.wireOp",EDGE,"E64")])]})});
            var Q2;
            Q2=makeQuery(id+"F21.boolean.opBoolean","COPY",EDGE,{"derivedFrom":makeQuery(id+"F21.opExtrude","SWEPT_EDGE",EDGE,{"disambiguationData":[OSD([sQuery(id+"F16.wireOp",EDGE,"E66"),sQuery(id+"F16.wireOp",EDGE,"E67")])]})});
            var Q3;
            Q3=makeQuery(id+"F21.boolean.opBoolean","COPY",EDGE,{"derivedFrom":makeQuery(id+"F21.opExtrude","SWEPT_EDGE",EDGE,{"disambiguationData":[OSD([sQuery(id+"F16.wireOp",EDGE,"E65"),sQuery(id+"F16.wireOp",EDGE,"E66")])]})});
            fillet(context, id + "F22", {"entities" : qUnion([Q0, Q1, Q2, Q3]), "radius" : 4 * mm, "tangentPropagation" : true, "allowEdgeOverflow" : false});
        }
    });
